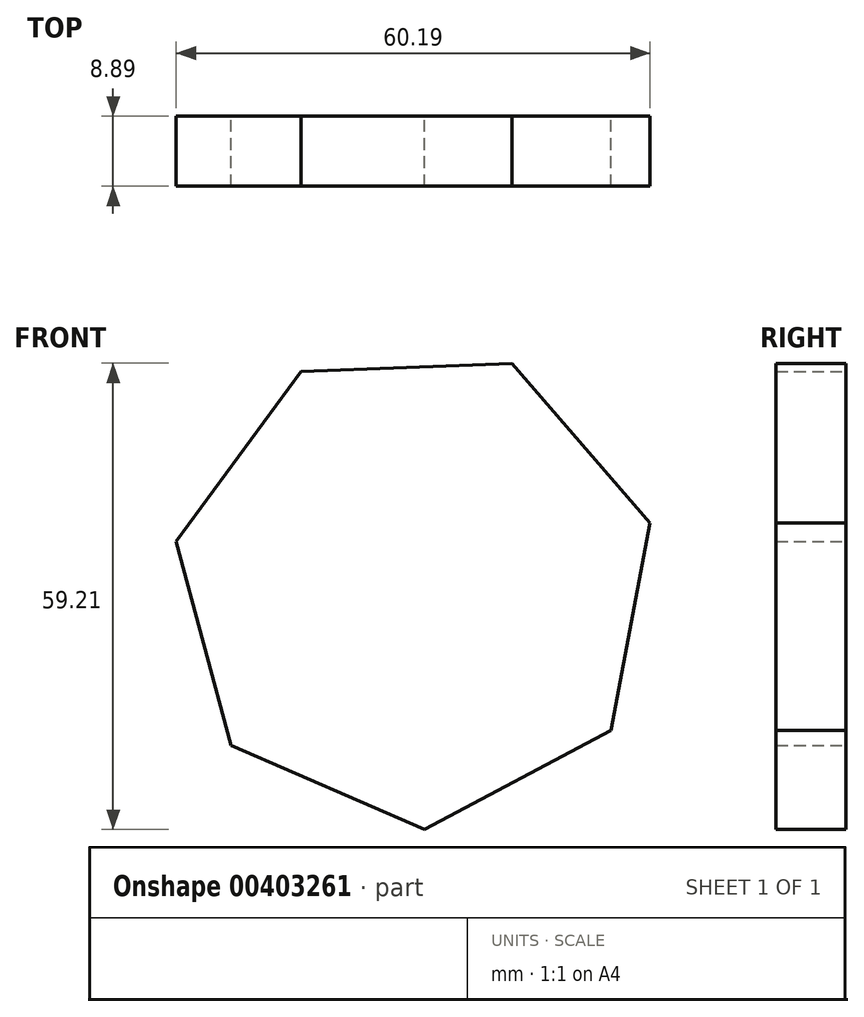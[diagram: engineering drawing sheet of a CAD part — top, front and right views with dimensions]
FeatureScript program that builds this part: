
annotation { "Feature Type Name" : "Feature", "Feature Type Description" : "" }
export const myFeature = defineFeature(function(context is Context, id is Id, definition is map)
    precondition{}
    {
        {
            var Q0;
            Q0=qCreatedBy(makeId("Front.planeOp"),FACE);
            var sketch = newSketch(context, id + "F0", { "sketchPlane" : qUnion([Q0])});
            skCircle(sketch, "E0.cCircle", {"center": v(0, 0) * mm, "radius": 27.83 * mm, "construction": true});
            skLineSegment(sketch, "E0.0", {"start": v(24.89, -18.3) * mm, "end": v(1.2, -30.87) * mm});
            skLineSegment(sketch, "E0.1", {"start": v(1.2, -30.87) * mm, "end": v(-23.38, -20.19) * mm});
            skLineSegment(sketch, "E0.2", {"start": v(-23.38, -20.19) * mm, "end": v(-30.36, 5.7) * mm});
            skLineSegment(sketch, "E0.3", {"start": v(-30.36, 5.7) * mm, "end": v(-14.48, 27.29) * mm});
            skLineSegment(sketch, "E0.4", {"start": v(-14.48, 27.29) * mm, "end": v(12.3, 28.34) * mm});
            skLineSegment(sketch, "E0.5", {"start": v(12.3, 28.34) * mm, "end": v(29.83, 8.04) * mm});
            skLineSegment(sketch, "E0.6", {"start": v(29.83, 8.04) * mm, "end": v(24.89, -18.3) * mm});
            skPoint(sketch, "E0.0.midPoint", {"position": v(13.05, -24.59) * mm});
            skSolve(sketch);
        }
        {
            var Q0;
            Q0=makeQuery(id+"F0.imprint","IMPRINT",FACE,{"disambiguationData":[TD([[makeQuery(id+"F0.imprint","IMPRINT",EDGE,{"derivedFrom":sQuery(id+"F0.wireOp",EDGE,"E0.0")}),-1.0]])]});
            extrude(context, id + "F1", {"entities" : qUnion([Q0]), "depth" : 8.9 * mm});
        }
    });
